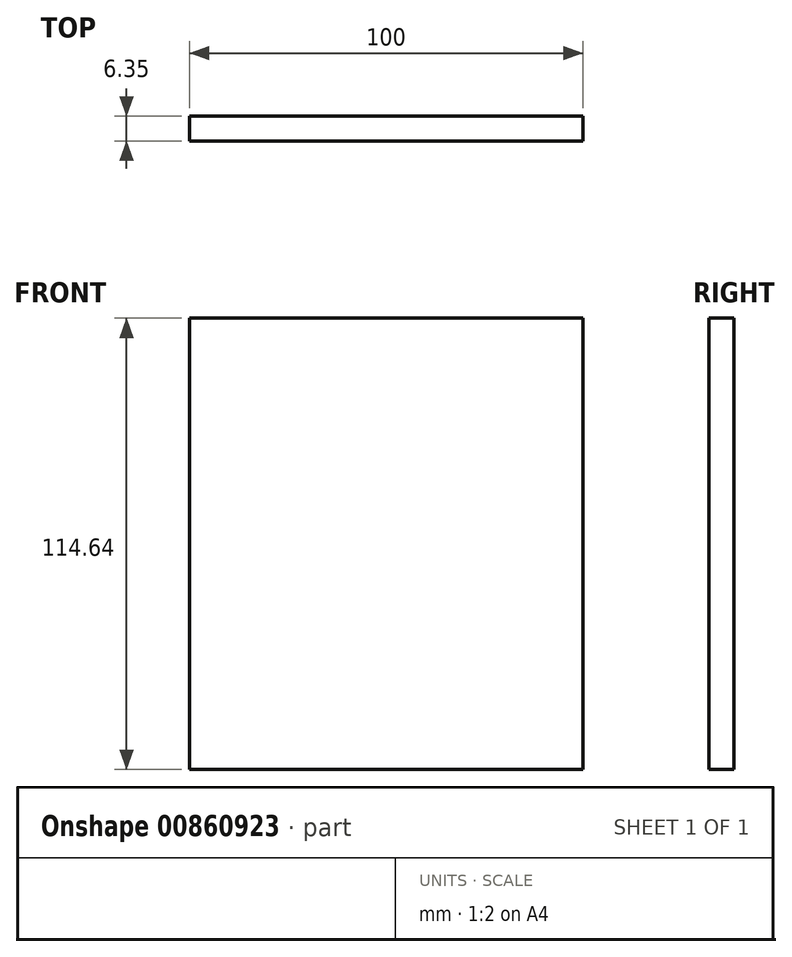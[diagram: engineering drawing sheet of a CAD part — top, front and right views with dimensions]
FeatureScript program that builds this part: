
annotation { "Feature Type Name" : "Feature", "Feature Type Description" : "" }
export const myFeature = defineFeature(function(context is Context, id is Id, definition is map)
    precondition{}
    {
        {
            var Q0;
            Q0=qCreatedBy(makeId("Front.planeOp"),FACE);
            var sketch = newSketch(context, id + "F0", { "sketchPlane" : qUnion([Q0])});
            skLineSegment(sketch, "E0.top", {"start": v(50, -50) * mm, "end": v(-50, -50) * mm});
            skLineSegment(sketch, "E0.left", {"start": v(50, 50) * mm, "end": v(50, -50) * mm});
            skLineSegment(sketch, "E0.right", {"start": v(-50, 50) * mm, "end": v(-50, -50) * mm});
            skPoint(sketch, "E0.middle", {"position": v(0, 0) * mm});
            skLineSegment(sketch, "E1", {"start": v(-50, 50) * mm, "end": v(-50, 64.64) * mm});
            skLineSegment(sketch, "E2", {"start": v(-50, 64.64) * mm, "end": v(50, 64.64) * mm});
            skLineSegment(sketch, "E3", {"start": v(50, 64.64) * mm, "end": v(50, 50) * mm});
            skSolve(sketch);
        }
        {
            var Q0;
            Q0=makeQuery(id+"F0.imprint","IMPRINT",FACE,{"disambiguationData":[TD([[makeQuery(id+"F0.imprint","IMPRINT",EDGE,{"derivedFrom":sQuery(id+"F0.wireOp",EDGE,"E0.bottom")}),1.0]])]});
            var Q1;
            Q1=makeQuery(id+"F0.imprint","IMPRINT",FACE,{"disambiguationData":[TD([[makeQuery(id+"F0.imprint","IMPRINT",EDGE,{"derivedFrom":sQuery(id+"F0.wireOp",EDGE,"E0.bottom")}),-1.0]])]});
            var Q2;
            Q2=makeQuery(id+"F0.imprint","IMPRINT",FACE,{"disambiguationData":[TD([[makeQuery(id+"F0.imprint","IMPRINT",EDGE,{"derivedFrom":sQuery(id+"F0.wireOp",EDGE,"E0.top")}),-1.0]])]});
            extrude(context, id + "F1", {"entities" : qUnion([Q0, Q1, Q2]), "depth" : 6.35 * mm, "offsetDistance" : 25 * mm});
        }
    });
